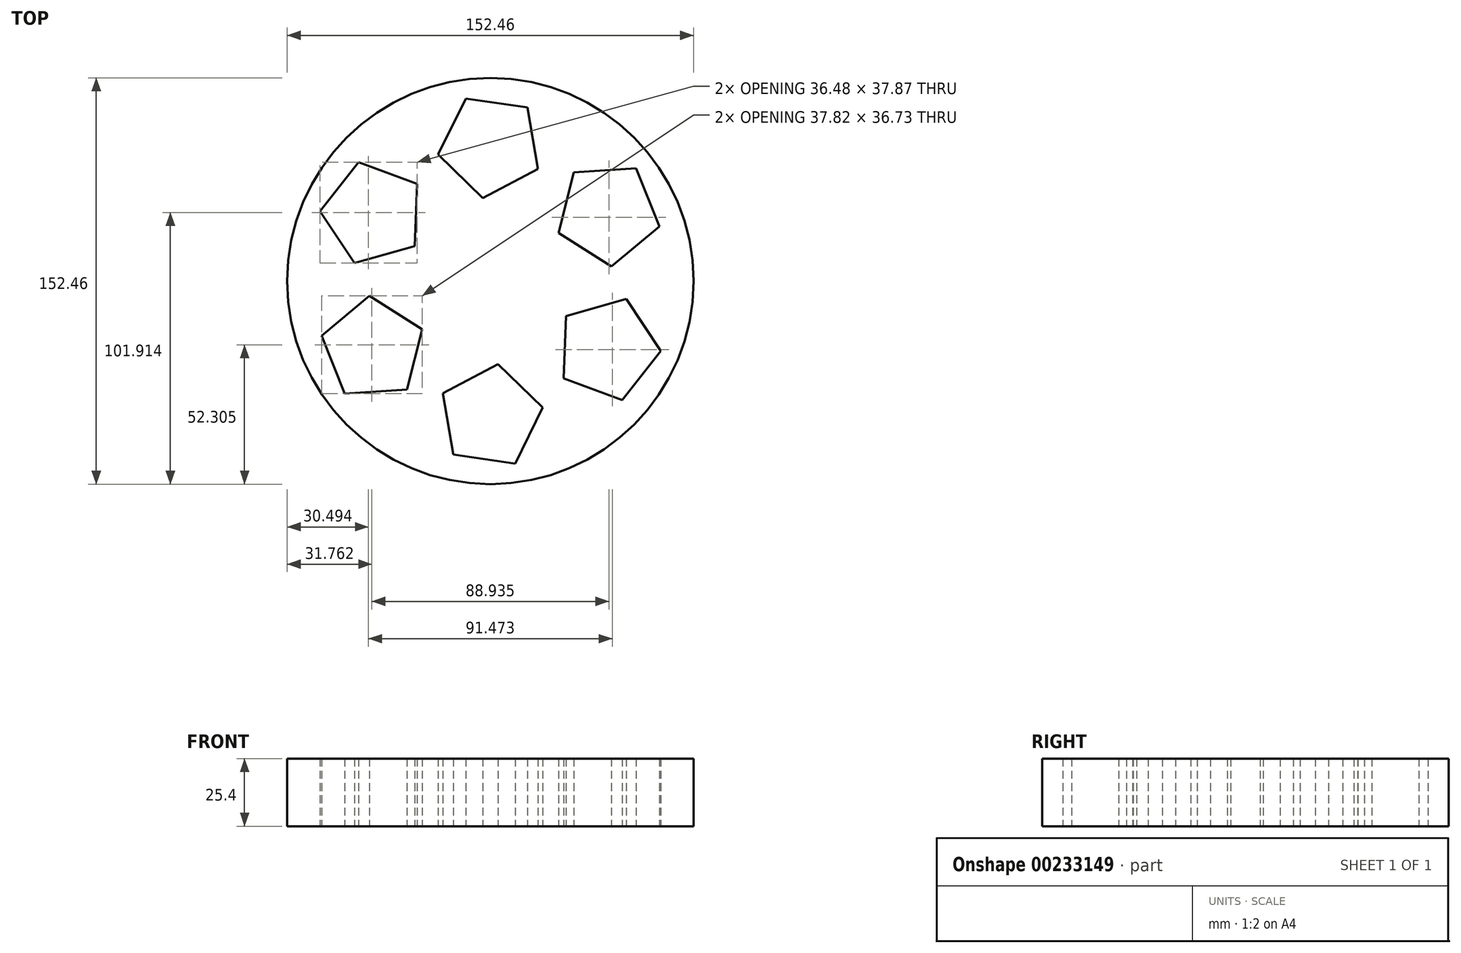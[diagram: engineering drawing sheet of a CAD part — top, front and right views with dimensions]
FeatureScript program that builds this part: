
annotation { "Feature Type Name" : "Feature", "Feature Type Description" : "" }
export const myFeature = defineFeature(function(context is Context, id is Id, definition is map)
    precondition{}
    {
        {
            var Q0;
            Q0=qCreatedBy(makeId("Top.planeOp"),FACE);
            var sketch = newSketch(context, id + "F0", { "sketchPlane" : qUnion([Q0])});
            skCircle(sketch, "E0", {"center": v(0, 0) * mm, "radius": 76.23 * mm});
            skCircle(sketch, "E1.cCircle", {"center": v(0, 50.88) * mm, "radius": 19.93 * mm, "construction": true});
            skLineSegment(sketch, "E1.0", {"start": v(-19.64, 47.51) * mm, "end": v(-9.28, 68.52) * mm});
            skLineSegment(sketch, "E1.1", {"start": v(-9.28, 68.52) * mm, "end": v(13.9, 65.15) * mm});
            skLineSegment(sketch, "E1.2", {"start": v(13.9, 65.15) * mm, "end": v(17.87, 42.07) * mm});
            skLineSegment(sketch, "E1.3", {"start": v(17.87, 42.07) * mm, "end": v(-2.86, 31.16) * mm});
            skLineSegment(sketch, "E1.4", {"start": v(-2.86, 31.16) * mm, "end": v(-19.64, 47.51) * mm});
            skLineSegment(sketch, "E2.1.0", {"start": v(63.38, 20.53) * mm, "end": v(45.37, 5.56) * mm});
            skLineSegment(sketch, "E2.1.1", {"start": v(54.7, 42.3) * mm, "end": v(63.38, 20.53) * mm});
            skLineSegment(sketch, "E2.1.2", {"start": v(31.33, 40.76) * mm, "end": v(54.7, 42.3) * mm});
            skLineSegment(sketch, "E2.1.3", {"start": v(25.56, 18.06) * mm, "end": v(31.33, 40.76) * mm});
            skLineSegment(sketch, "E2.1.4", {"start": v(45.37, 5.56) * mm, "end": v(25.56, 18.06) * mm});
            skLineSegment(sketch, "E2.2.0", {"start": v(49.47, -44.62) * mm, "end": v(27.5, -36.5) * mm});
            skLineSegment(sketch, "E2.2.1", {"start": v(63.98, -26.23) * mm, "end": v(49.47, -44.62) * mm});
            skLineSegment(sketch, "E2.2.2", {"start": v(50.96, -6.75) * mm, "end": v(63.98, -26.23) * mm});
            skLineSegment(sketch, "E2.2.3", {"start": v(28.42, -13.1) * mm, "end": v(50.96, -6.75) * mm});
            skLineSegment(sketch, "E2.2.4", {"start": v(27.5, -36.5) * mm, "end": v(28.42, -13.1) * mm});
            skLineSegment(sketch, "E2.3.0", {"start": v(-13.9, -65.15) * mm, "end": v(-17.87, -42.07) * mm});
            skLineSegment(sketch, "E2.3.1", {"start": v(9.28, -68.52) * mm, "end": v(-13.9, -65.15) * mm});
            skLineSegment(sketch, "E2.3.2", {"start": v(19.64, -47.51) * mm, "end": v(9.28, -68.52) * mm});
            skLineSegment(sketch, "E2.3.3", {"start": v(2.86, -31.16) * mm, "end": v(19.64, -47.51) * mm});
            skLineSegment(sketch, "E2.3.4", {"start": v(-17.87, -42.07) * mm, "end": v(2.86, -31.16) * mm});
            skLineSegment(sketch, "E2.4.0", {"start": v(-63.38, -20.53) * mm, "end": v(-45.37, -5.56) * mm});
            skLineSegment(sketch, "E2.4.1", {"start": v(-54.7, -42.3) * mm, "end": v(-63.38, -20.53) * mm});
            skLineSegment(sketch, "E2.4.2", {"start": v(-31.33, -40.76) * mm, "end": v(-54.7, -42.3) * mm});
            skLineSegment(sketch, "E2.4.3", {"start": v(-25.56, -18.06) * mm, "end": v(-31.33, -40.76) * mm});
            skLineSegment(sketch, "E2.4.4", {"start": v(-45.37, -5.56) * mm, "end": v(-25.56, -18.06) * mm});
            skLineSegment(sketch, "E2.5.0", {"start": v(-49.47, 44.62) * mm, "end": v(-27.5, 36.5) * mm});
            skLineSegment(sketch, "E2.5.1", {"start": v(-63.98, 26.23) * mm, "end": v(-49.47, 44.62) * mm});
            skLineSegment(sketch, "E2.5.2", {"start": v(-50.96, 6.75) * mm, "end": v(-63.98, 26.23) * mm});
            skLineSegment(sketch, "E2.5.3", {"start": v(-28.42, 13.1) * mm, "end": v(-50.96, 6.75) * mm});
            skLineSegment(sketch, "E2.5.4", {"start": v(-27.5, 36.5) * mm, "end": v(-28.42, 13.1) * mm});
            skLineSegment(sketch, "E2.anchor1", {"start": v(0, 0) * mm, "end": v(-19.64, 47.51) * mm, "construction": true});
            skLineSegment(sketch, "E2.anchor2", {"start": v(0, 0) * mm, "end": v(-50.96, 6.75) * mm, "construction": true});
            skSolve(sketch);
        }
        {
            var Q0;
            Q0 = qSketchRegion(id + "F0", true);
            extrude(context, id + "F1", {"entities" : qUnion([Q0]), "depth" : 25.4 * mm});
        }
    });
